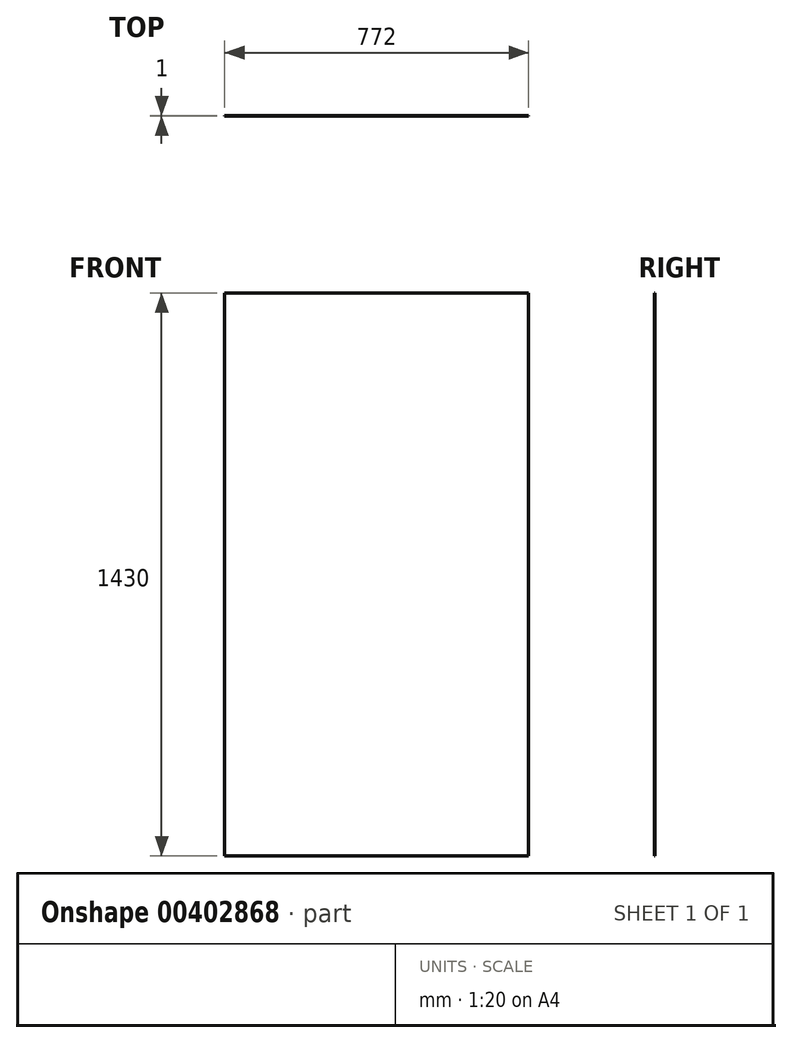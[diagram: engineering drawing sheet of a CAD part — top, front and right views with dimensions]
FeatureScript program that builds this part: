
annotation { "Feature Type Name" : "Feature", "Feature Type Description" : "" }
export const myFeature = defineFeature(function(context is Context, id is Id, definition is map)
    precondition{}
    {
        {
            var Q0;
            Q0=qCreatedBy(makeId("Front.planeOp"),FACE);
            var sketch = newSketch(context, id + "F0", { "sketchPlane" : qUnion([Q0])});
            skLineSegment(sketch, "E0.bottom", {"start": v(-386, 715) * mm, "end": v(386, 715) * mm});
            skLineSegment(sketch, "E0.top", {"start": v(-386, -715) * mm, "end": v(386, -715) * mm});
            skLineSegment(sketch, "E0.left", {"start": v(-386, 715) * mm, "end": v(-386, -715) * mm});
            skLineSegment(sketch, "E0.right", {"start": v(386, 715) * mm, "end": v(386, -715) * mm});
            skPoint(sketch, "E0.middle", {"position": v(0, 0) * mm});
            skSolve(sketch);
        }
        {
            var Q0;
            Q0=makeQuery(id+"F0.imprint","IMPRINT",FACE,{"disambiguationData":[TD([[makeQuery(id+"F0.imprint","IMPRINT",EDGE,{"derivedFrom":sQuery(id+"F0.wireOp",EDGE,"E0.bottom")}),-1.0]])]});
            extrude(context, id + "F1", {"entities" : qUnion([Q0]), "depth" : 1 * mm});
        }
    });
